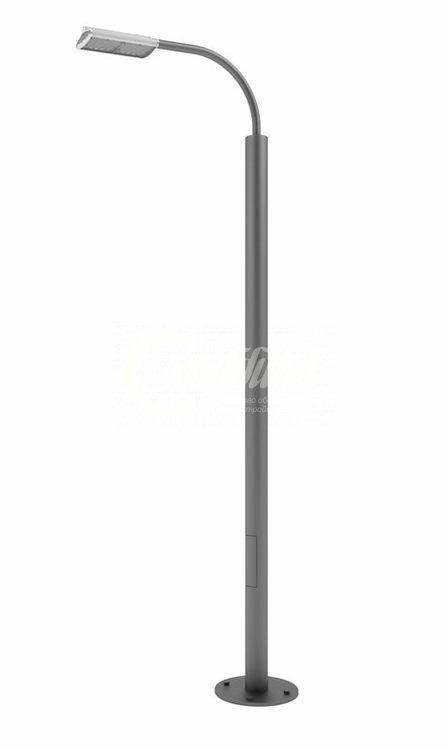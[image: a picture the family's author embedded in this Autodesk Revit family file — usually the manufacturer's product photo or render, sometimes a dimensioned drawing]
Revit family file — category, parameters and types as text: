
# Revit family: Стальной фонарный столб «Техно-Э» со светильником Арт 10234
name_source: partatom
category: Антураж
revit_build: Autodesk Revit 2018 (Build: 20180423_1000(x64)
units: mm (PartAtom-declared; Revit-internal decimal feet)

## family parameters
Всегда вертикально = Да
Источник визуального образа = Геометрия семейства
На основе рабочей плоскости = Нет
Общий = Нет
При загрузке вырезать с полостями = Нет
Точка расчета площади = Нет

## types (4) — shared parameters
URL = https://hobbyka.ru
Артикул товара = Арт 10234
Группа модели = Светильники со стальными опорами
Длина = 1500 мм
Изготовитель = ООО «Хоббика»
Изображение типоразмера = Стальной фонарный столб «Техно-Э» со светильником Арт 10234.jpg
Материал изделия = Сталь
Цвет каркаса = Сталь
Ширина = 200 мм

## per-type parameters (varying)
| type | Высота | Высота опоры | Модель 3,2 м | Модель 4,2 м | Модель 5,2 м | Описание |
| Версия 3,2 (80 Вт) | 3200 мм | 2500 мм | Да | Нет | Нет | Стальной фонарный столб «Техно-Э» со светильником. Модель 3,2 м (80 Вт) |
| Версия 4,2 (120 Вт) | 4200 мм | 3500 мм | Нет | Да | Нет | Стальной фонарный столб «Техно-Э» со светильником. Модель 4,2 м (120 Вт) |
| Версия 5,2 (160 Вт) | 5200 мм | 4500 мм | Нет | Нет | Да | Стальной фонарный столб «Техно-Э» со светильником. Модель 5,2 м (160 Вт) |
| Версия 6,2 (160 Вт) | 6200 мм | 5500 мм | Нет | Нет | Нет | Стальной фонарный столб «Техно-Э» со светильником. Модель 6,2 м (160 Вт) |
